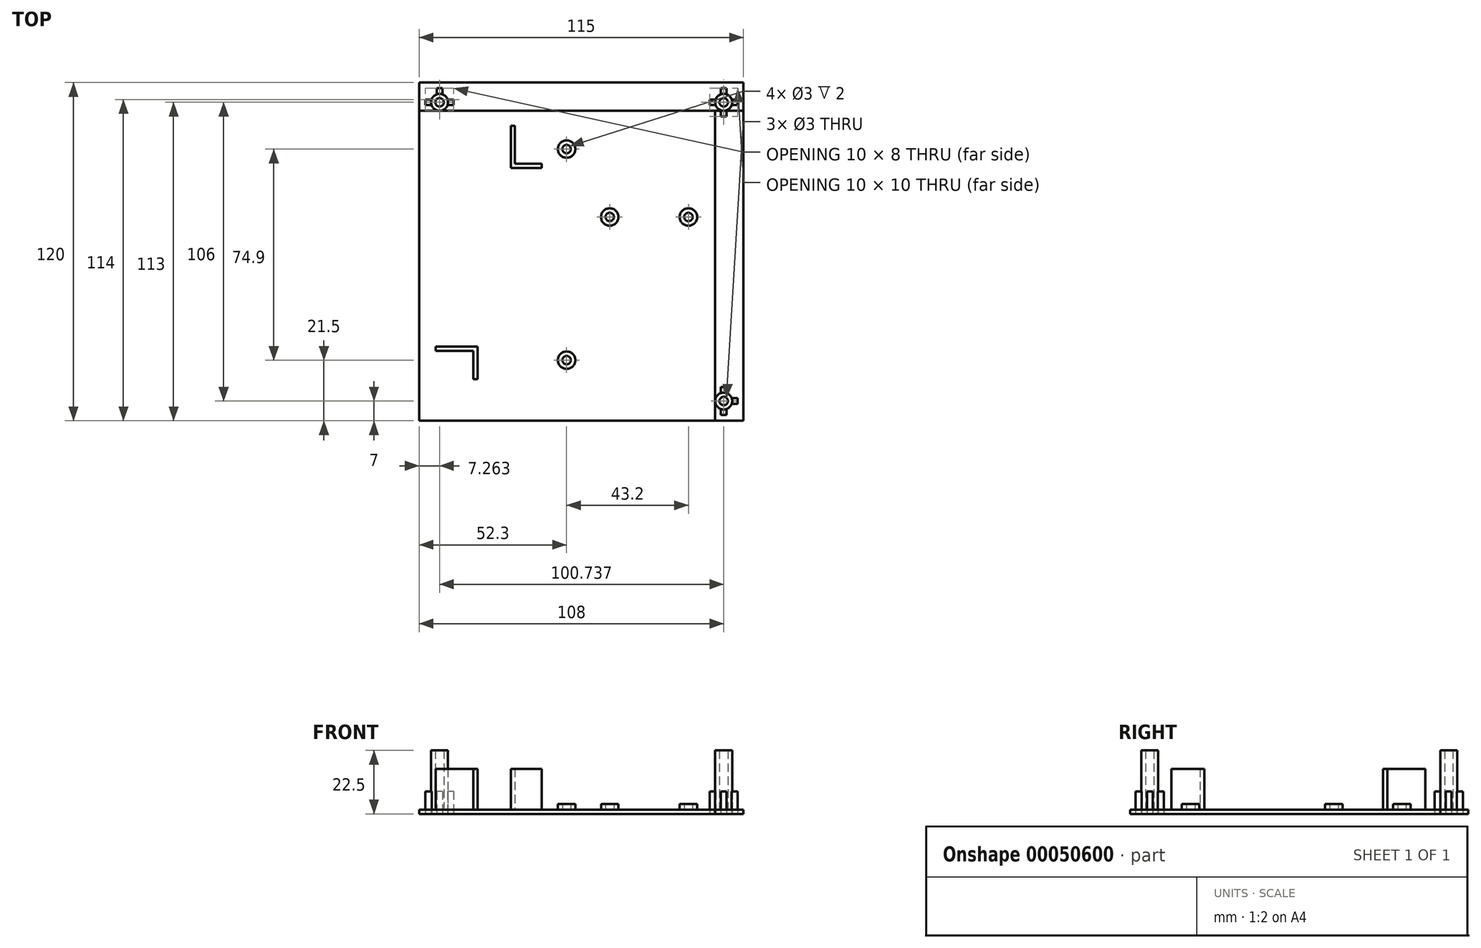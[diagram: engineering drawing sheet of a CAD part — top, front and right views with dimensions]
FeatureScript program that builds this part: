
annotation { "Feature Type Name" : "Feature", "Feature Type Description" : "" }
export const myFeature = defineFeature(function(context is Context, id is Id, definition is map)
    precondition{}
    {
        {
            var Q0;
            Q0=qCreatedBy(makeId("Top.planeOp"),FACE);
            var sketch = newSketch(context, id + "F0", { "sketchPlane" : qUnion([Q0])});
            skLineSegment(sketch, "E0.rect.bottom", {"start": v(52.5, 55) * mm, "end": v(-52.5, 55) * mm});
            skLineSegment(sketch, "E0.rect.top", {"start": v(52.5, -55) * mm, "end": v(-52.5, -55) * mm});
            skLineSegment(sketch, "E0.rect.left", {"start": v(52.5, 55) * mm, "end": v(52.5, -55) * mm});
            skLineSegment(sketch, "E0.rect.right", {"start": v(-52.5, 55) * mm, "end": v(-52.5, -55) * mm});
            skPoint(sketch, "E0.rect.middle", {"position": v(0, 0) * mm});
            skSolve(sketch);
        }
        {
            var Q0;
            Q0=makeQuery(id+"F0.imprint","IMPRINT",FACE,{"disambiguationData":[TD([[makeQuery(id+"F0.imprint","IMPRINT",EDGE,{"derivedFrom":sQuery(id+"F0.wireOp",EDGE,"E0.rect.bottom")}),1.0]])]});
            extrude(context, id + "F1", {"entities" : qUnion([Q0]), "depth" : 1.5 * mm});
        }
        {
            var Q0;
            Q0=makeQuery(id+"F1.opExtrude","CAP_FACE",FACE,{"disambiguationData":[OSD([sQuery(id+"F0.wireOp",EDGE,"E0.rect.bottom"),sQuery(id+"F0.wireOp",EDGE,"E0.rect.top"),sQuery(id+"F0.wireOp",EDGE,"E0.rect.left"),sQuery(id+"F0.wireOp",EDGE,"E0.rect.right")])],"isStart":false});
            var sketch = newSketch(context, id + "F2", { "sketchPlane" : qUnion([Q0])});
            skCircle(sketch, "E1", {"center": v(-0.2, 41.4) * mm, "radius": 3.1 * mm});
            skCircle(sketch, "E2", {"center": v(-0.2, 41.4) * mm, "radius": 1.5 * mm});
            skCircle(sketch, "E3", {"center": v(-0.2, -33.5) * mm, "radius": 3.1 * mm});
            skCircle(sketch, "E4", {"center": v(-0.2, -33.5) * mm, "radius": 1.5 * mm});
            skCircle(sketch, "E5", {"center": v(43, 17.3) * mm, "radius": 3.1 * mm});
            skCircle(sketch, "E6", {"center": v(43, 17.3) * mm, "radius": 1.5 * mm});
            skCircle(sketch, "E7", {"center": v(15.1, 17.3) * mm, "radius": 3.1 * mm});
            skCircle(sketch, "E8", {"center": v(15.1, 17.3) * mm, "radius": 1.5 * mm});
            skLineSegment(sketch, "E9", {"start": v(-20, 49.73) * mm, "end": v(-20, 34.73) * mm});
            skLineSegment(sketch, "E10", {"start": v(-20, 34.73) * mm, "end": v(-9, 34.73) * mm});
            skLineSegment(sketch, "E11", {"start": v(-9, 34.73) * mm, "end": v(-9, 36.23) * mm});
            skLineSegment(sketch, "E12", {"start": v(-9, 36.23) * mm, "end": v(-18.5, 36.23) * mm});
            skLineSegment(sketch, "E13", {"start": v(-18.5, 36.23) * mm, "end": v(-18.5, 49.73) * mm});
            skLineSegment(sketch, "E14", {"start": v(-18.5, 49.73) * mm, "end": v(-20, 49.73) * mm});
            skLineSegment(sketch, "E15", {"start": v(-46.6, -28.7) * mm, "end": v(-31.8, -28.7) * mm});
            skLineSegment(sketch, "E16", {"start": v(-31.8, -28.7) * mm, "end": v(-31.8, -40.3) * mm});
            skLineSegment(sketch, "E17", {"start": v(-31.8, -40.3) * mm, "end": v(-33.3, -40.3) * mm});
            skLineSegment(sketch, "E18", {"start": v(-33.3, -40.3) * mm, "end": v(-33.3, -30.2) * mm});
            skLineSegment(sketch, "E19", {"start": v(-33.3, -30.2) * mm, "end": v(-46.6, -30.2) * mm});
            skLineSegment(sketch, "E20", {"start": v(-46.6, -30.2) * mm, "end": v(-46.6, -28.7) * mm});
            skSolve(sketch);
        }
        {
            var Q0;
            Q0=makeQuery(id+"F2.imprint","IMPRINT",FACE,{"disambiguationData":[TD([[makeQuery(id+"F2.imprint","IMPRINT",EDGE,{"derivedFrom":sQuery(id+"F2.wireOp",EDGE,"E1")}),1.0]])]});
            var Q1;
            Q1=makeQuery(id+"F2.imprint","IMPRINT",FACE,{"disambiguationData":[TD([[makeQuery(id+"F2.imprint","IMPRINT",EDGE,{"derivedFrom":sQuery(id+"F2.wireOp",EDGE,"E7")}),1.0]])]});
            var Q2;
            Q2=makeQuery(id+"F2.imprint","IMPRINT",FACE,{"disambiguationData":[TD([[makeQuery(id+"F2.imprint","IMPRINT",EDGE,{"derivedFrom":sQuery(id+"F2.wireOp",EDGE,"E5")}),1.0]])]});
            var Q3;
            Q3=makeQuery(id+"F2.imprint","IMPRINT",FACE,{"disambiguationData":[TD([[makeQuery(id+"F2.imprint","IMPRINT",EDGE,{"derivedFrom":sQuery(id+"F2.wireOp",EDGE,"E3")}),1.0]])]});
            extrude(context, id + "F3", {"entities" : qUnion([Q0, Q1, Q2, Q3]), "operationType" : NewBodyOperationType.ADD, "depth" : 2 * mm});
        }
        {
            var Q0;
            Q0=makeQuery(id+"F2.imprint","IMPRINT",FACE,{"disambiguationData":[TD([[makeQuery(id+"F2.imprint","IMPRINT",EDGE,{"derivedFrom":sQuery(id+"F2.wireOp",EDGE,"E9")}),1.0]])]});
            extrude(context, id + "F4", {"entities" : qUnion([Q0]), "operationType" : NewBodyOperationType.ADD, "depth" : 14.5 * mm});
        }
        {
            var Q0;
            Q0=makeQuery(id+"F2.imprint","IMPRINT",FACE,{"disambiguationData":[TD([[makeQuery(id+"F2.imprint","IMPRINT",EDGE,{"derivedFrom":sQuery(id+"F2.wireOp",EDGE,"E15")}),-1.0]])]});
            extrude(context, id + "F5", {"entities" : qUnion([Q0]), "operationType" : NewBodyOperationType.ADD, "depth" : 14.5 * mm});
        }
        {
            var Q0;
            Q0=qCreatedBy(makeId("Top.planeOp"),FACE);
            var sketch = newSketch(context, id + "F6", { "sketchPlane" : qUnion([Q0])});
            skLineSegment(sketch, "E21.bottom", {"start": v(-52.5, 55) * mm, "end": v(62.5, 55) * mm});
            skLineSegment(sketch, "E21.top", {"start": v(-52.5, 65) * mm, "end": v(62.5, 65) * mm});
            skLineSegment(sketch, "E21.left", {"start": v(-52.5, 55) * mm, "end": v(-52.5, 65) * mm});
            skLineSegment(sketch, "E21.right", {"start": v(62.5, 55) * mm, "end": v(62.5, 65) * mm});
            skLineSegment(sketch, "E22.bottom", {"start": v(62.5, 55) * mm, "end": v(52.5, 55) * mm});
            skLineSegment(sketch, "E22.top", {"start": v(62.5, -55) * mm, "end": v(52.5, -55) * mm});
            skLineSegment(sketch, "E22.left", {"start": v(62.5, 55) * mm, "end": v(62.5, -55) * mm});
            skLineSegment(sketch, "E22.right", {"start": v(52.5, 55) * mm, "end": v(52.5, -55) * mm});
            skCircle(sketch, "E23", {"center": v(-45.24, 58) * mm, "radius": 3 * mm});
            skCircle(sketch, "E24", {"center": v(-45.24, 58) * mm, "radius": 1.5 * mm});
            skLineSegment(sketch, "E25.rect.bottom", {"start": v(-44.24, 63) * mm, "end": v(-46.24, 63) * mm});
            skLineSegment(sketch, "E25.rect.left", {"start": v(-44.24, 63) * mm, "end": v(-44.24, 60.83) * mm});
            skLineSegment(sketch, "E25.rect.right", {"start": v(-46.24, 63) * mm, "end": v(-46.24, 60.83) * mm});
            skPoint(sketch, "E25.rect.middle", {"position": v(-45.24, 61) * mm});
            skLineSegment(sketch, "E26.rect.right", {"start": v(-50.24, 59) * mm, "end": v(-50.24, 57) * mm});
            skPoint(sketch, "E26.rect.middle", {"position": v(-48.24, 58) * mm});
            skLineSegment(sketch, "E27.rect.bottom", {"start": v(-44.24, 53) * mm, "end": v(-46.24, 53) * mm});
            skLineSegment(sketch, "E27.rect.left", {"start": v(-44.24, 53) * mm, "end": v(-44.24, 55.17) * mm});
            skLineSegment(sketch, "E27.rect.right", {"start": v(-46.24, 53) * mm, "end": v(-46.24, 55.17) * mm});
            skPoint(sketch, "E27.rect.middle", {"position": v(-45.24, 55) * mm});
            skLineSegment(sketch, "E28.rect.bottom", {"start": v(-40.24, 59) * mm, "end": v(-42.4, 59) * mm});
            skLineSegment(sketch, "E28.rect.top", {"start": v(-40.24, 57) * mm, "end": v(-42.4, 57) * mm});
            skLineSegment(sketch, "E28.rect.left", {"start": v(-40.24, 59) * mm, "end": v(-40.24, 57) * mm});
            skPoint(sketch, "E28.rect.middle", {"position": v(-42.24, 58) * mm});
            skPoint(sketch, "E29.trimOffspring.end.orphan", {"position": v(-44.24, 57) * mm});
            skLineSegment(sketch, "E30.trimOffspring", {"start": v(-48.06, 57) * mm, "end": v(-50.24, 57) * mm});
            skPoint(sketch, "E26.rect.top.start.orphan", {"position": v(-46.24, 57) * mm});
            skLineSegment(sketch, "E31.trimOffspring", {"start": v(-48.06, 59) * mm, "end": v(-50.24, 59) * mm});
            skPoint(sketch, "E26.rect.bottom.start.orphan", {"position": v(-46.24, 59) * mm});
            skPoint(sketch, "E32.orphan", {"position": v(-44.24, 59) * mm});
            skCircle(sketch, "E33", {"center": v(55.5, 58) * mm, "radius": 3 * mm});
            skCircle(sketch, "E34", {"center": v(55.5, 58) * mm, "radius": 1.5 * mm});
            skLineSegment(sketch, "E35.rect.bottom", {"start": v(56.5, 63) * mm, "end": v(54.5, 63) * mm});
            skLineSegment(sketch, "E35.rect.left", {"start": v(56.5, 63) * mm, "end": v(56.5, 60.83) * mm});
            skLineSegment(sketch, "E35.rect.right", {"start": v(54.5, 63) * mm, "end": v(54.5, 60.83) * mm});
            skPoint(sketch, "E35.rect.middle", {"position": v(55.5, 61) * mm});
            skLineSegment(sketch, "E36.rect.bottom", {"start": v(60.5, 59) * mm, "end": v(58.33, 59) * mm});
            skLineSegment(sketch, "E36.rect.top", {"start": v(60.5, 57) * mm, "end": v(58.33, 57) * mm});
            skLineSegment(sketch, "E36.rect.left", {"start": v(60.5, 59) * mm, "end": v(60.5, 57) * mm});
            skPoint(sketch, "E36.rect.middle", {"position": v(58.5, 58) * mm});
            skLineSegment(sketch, "E37.rect.bottom", {"start": v(56.5, 53) * mm, "end": v(54.5, 53) * mm});
            skLineSegment(sketch, "E37.rect.left", {"start": v(56.5, 53) * mm, "end": v(56.5, 55.17) * mm});
            skLineSegment(sketch, "E37.rect.right", {"start": v(54.5, 53) * mm, "end": v(54.5, 55.17) * mm});
            skPoint(sketch, "E37.rect.middle", {"position": v(55.5, 55) * mm});
            skLineSegment(sketch, "E38.rect.right", {"start": v(50.5, 59) * mm, "end": v(50.5, 57) * mm});
            skPoint(sketch, "E38.rect.middle", {"position": v(52.5, 58) * mm});
            skLineSegment(sketch, "E39.trimOffspring", {"start": v(52.67, 59) * mm, "end": v(50.5, 59) * mm});
            skLineSegment(sketch, "E40.trimOffspring", {"start": v(52.67, 57) * mm, "end": v(50.5, 57) * mm});
            skPoint(sketch, "E38.rect.bottom.start.orphan", {"position": v(54.5, 59) * mm});
            skPoint(sketch, "E38.rect.top.start.orphan", {"position": v(54.5, 57) * mm});
            skPoint(sketch, "E41.trimOffspring.end.orphan", {"position": v(56.5, 57) * mm});
            skPoint(sketch, "E42.orphan", {"position": v(56.5, 59) * mm});
            skCircle(sketch, "E43", {"center": v(55.5, -48) * mm, "radius": 3 * mm});
            skCircle(sketch, "E44", {"center": v(55.5, -48) * mm, "radius": 1.5 * mm});
            skLineSegment(sketch, "E45.rect.bottom", {"start": v(56.5, -53) * mm, "end": v(54.5, -53) * mm});
            skLineSegment(sketch, "E45.rect.left", {"start": v(56.5, -53) * mm, "end": v(56.5, -50.83) * mm});
            skLineSegment(sketch, "E45.rect.right", {"start": v(54.5, -53) * mm, "end": v(54.5, -50.83) * mm});
            skPoint(sketch, "E45.rect.middle", {"position": v(55.5, -51) * mm});
            skLineSegment(sketch, "E46.rect.bottom", {"start": v(60.5, -47) * mm, "end": v(58.33, -47) * mm});
            skLineSegment(sketch, "E46.rect.top", {"start": v(60.5, -49) * mm, "end": v(58.33, -49) * mm});
            skLineSegment(sketch, "E46.rect.left", {"start": v(60.5, -47) * mm, "end": v(60.5, -49) * mm});
            skPoint(sketch, "E46.rect.middle", {"position": v(58.5, -48) * mm});
            skLineSegment(sketch, "E47.rect.bottom", {"start": v(56.5, -43) * mm, "end": v(54.5, -43) * mm});
            skLineSegment(sketch, "E47.rect.left", {"start": v(56.5, -43) * mm, "end": v(56.5, -45.17) * mm});
            skLineSegment(sketch, "E47.rect.right", {"start": v(54.5, -43) * mm, "end": v(54.5, -45.17) * mm});
            skPoint(sketch, "E47.rect.middle", {"position": v(55.5, -45) * mm});
            skLineSegment(sketch, "E48.rect.right", {"start": v(50.5, -47) * mm, "end": v(50.5, -49) * mm});
            skPoint(sketch, "E48.rect.middle", {"position": v(52.5, -48) * mm});
            skLineSegment(sketch, "E49.trimOffspring", {"start": v(52.67, -49) * mm, "end": v(50.5, -49) * mm});
            skPoint(sketch, "E48.rect.top.start.orphan", {"position": v(54.5, -49) * mm});
            skPoint(sketch, "E50.trimOffspring.end.orphan", {"position": v(56.5, -49) * mm});
            skLineSegment(sketch, "E51.trimOffspring", {"start": v(52.67, -47) * mm, "end": v(50.5, -47) * mm});
            skPoint(sketch, "E48.rect.bottom.start.orphan", {"position": v(54.5, -47) * mm});
            skPoint(sketch, "E52.trimOffspring.end.orphan", {"position": v(56.5, -47) * mm});
            skSolve(sketch);
        }
        {
            var Q0;
            Q0=makeQuery(id+"F6.imprint","IMPRINT",FACE,{"disambiguationData":[TD([[makeQuery(id+"F6.imprint","IMPRINT",EDGE,{"derivedFrom":sQuery(id+"F6.wireOp",EDGE,"E21.bottom")}),1.0]])]});
            var Q1;
            Q1=makeQuery(id+"F6.imprint","IMPRINT",FACE,{"disambiguationData":[TD([[makeQuery(id+"F6.imprint","IMPRINT",EDGE,{"derivedFrom":sQuery(id+"F6.wireOp",EDGE,"E22.bottom")}),1.0]])]});
            extrude(context, id + "F7", {"entities" : qUnion([Q0, Q1]), "operationType" : NewBodyOperationType.ADD, "depth" : 1.5 * mm});
        }
        {
            var Q0;
            Q0=makeQuery(id+"F6.imprint","IMPRINT",FACE,{"disambiguationData":[TD([[makeQuery(id+"F6.imprint","IMPRINT",EDGE,{"derivedFrom":sQuery(id+"F6.wireOp",EDGE,"E24")}),-1.0]])]});
            extrude(context, id + "F8", {"entities" : qUnion([Q0]), "depth" : 22.5 * mm});
        }
        {
            var Q0;
            Q0=makeQuery(id+"F6.imprint","IMPRINT",FACE,{"disambiguationData":[TD([[makeQuery(id+"F6.imprint","IMPRINT",EDGE,{"derivedFrom":sQuery(id+"F6.wireOp",EDGE,"E25.rect.bottom")}),1.0]])]});
            var Q1;
            Q1=makeQuery(id+"F6.imprint","IMPRINT",FACE,{"disambiguationData":[TD([[makeQuery(id+"F6.imprint","IMPRINT",EDGE,{"derivedFrom":sQuery(id+"F6.wireOp",EDGE,"E26.rect.right")}),1.0]])]});
            var Q2;
            {var subQ0=sQuery(id+"F6.wireOp",EDGE,"E28.rect.bottom");Q2=makeQuery(id+"F6.imprint","IMPRINT",FACE,{"disambiguationData":[TD([[makeQuery(id+"F6.imprint","IMPRINT",EDGE,{"derivedFrom":subQ0}),1.0]])]});}
            extrude(context, id + "F9", {"entities" : qUnion([Q0, Q1, Q2]), "depth" : 8 * mm});
        }
        {
            var Q0;
            Q0=makeQuery(id+"F6.imprint","IMPRINT",FACE,{"disambiguationData":[TD([[makeQuery(id+"F6.imprint","IMPRINT",EDGE,{"derivedFrom":sQuery(id+"F6.wireOp",EDGE,"E34")}),-1.0]])]});
            extrude(context, id + "F10", {"entities" : qUnion([Q0]), "depth" : 22.5 * mm});
        }
        {
            var Q0;
            Q0=makeQuery(id+"F6.imprint","IMPRINT",FACE,{"disambiguationData":[TD([[makeQuery(id+"F6.imprint","IMPRINT",EDGE,{"derivedFrom":sQuery(id+"F6.wireOp",EDGE,"E38.rect.right")}),1.0]])]});
            var Q1;
            Q1=makeQuery(id+"F6.imprint","IMPRINT",FACE,{"disambiguationData":[TD([[makeQuery(id+"F6.imprint","IMPRINT",EDGE,{"derivedFrom":sQuery(id+"F6.wireOp",EDGE,"E35.rect.bottom")}),1.0]])]});
            var Q2;
            {var subQ0=sQuery(id+"F6.wireOp",EDGE,"E36.rect.bottom");Q2=makeQuery(id+"F6.imprint","IMPRINT",FACE,{"disambiguationData":[TD([[makeQuery(id+"F6.imprint","IMPRINT",EDGE,{"derivedFrom":subQ0}),1.0]])]});}
            var Q3;
            {var subQ0=sQuery(id+"F6.wireOp",EDGE,"E37.rect.bottom");Q3=makeQuery(id+"F6.imprint","IMPRINT",FACE,{"disambiguationData":[TD([[makeQuery(id+"F6.imprint","IMPRINT",EDGE,{"derivedFrom":subQ0}),-1.0]])]});}
            extrude(context, id + "F11", {"entities" : qUnion([Q0, Q1, Q2, Q3]), "depth" : 8 * mm});
        }
        {
            var Q0;
            Q0=makeQuery(id+"F6.imprint","IMPRINT",FACE,{"disambiguationData":[TD([[makeQuery(id+"F6.imprint","IMPRINT",EDGE,{"derivedFrom":sQuery(id+"F6.wireOp",EDGE,"E21.top")}),-1.0]])]});
            var Q1;
            Q1=makeQuery(id+"F6.imprint","IMPRINT",FACE,{"disambiguationData":[TD([[makeQuery(id+"F6.imprint","IMPRINT",EDGE,{"derivedFrom":sQuery(id+"F6.wireOp",EDGE,"E22.top")}),-1.0]])]});
            extrude(context, id + "F12", {"entities" : qUnion([Q0, Q1]), "depth" : 1.5 * mm});
        }
        {
            var Q0;
            Q0=makeQuery(id+"F6.imprint","IMPRINT",FACE,{"disambiguationData":[TD([[makeQuery(id+"F6.imprint","IMPRINT",EDGE,{"derivedFrom":sQuery(id+"F6.wireOp",EDGE,"E44")}),-1.0]])]});
            extrude(context, id + "F13", {"entities" : qUnion([Q0]), "depth" : 22.5 * mm});
        }
        {
            var Q0;
            Q0=makeQuery(id+"F6.imprint","IMPRINT",FACE,{"disambiguationData":[TD([[makeQuery(id+"F6.imprint","IMPRINT",EDGE,{"derivedFrom":sQuery(id+"F6.wireOp",EDGE,"E47.rect.bottom")}),1.0]])]});
            var Q1;
            {var subQ0=sQuery(id+"F6.wireOp",EDGE,"E46.rect.bottom");Q1=makeQuery(id+"F6.imprint","IMPRINT",FACE,{"disambiguationData":[TD([[makeQuery(id+"F6.imprint","IMPRINT",EDGE,{"derivedFrom":subQ0}),1.0]])]});}
            var Q2;
            Q2=makeQuery(id+"F6.imprint","IMPRINT",FACE,{"disambiguationData":[TD([[makeQuery(id+"F6.imprint","IMPRINT",EDGE,{"derivedFrom":sQuery(id+"F6.wireOp",EDGE,"E45.rect.bottom")}),-1.0]])]});
            extrude(context, id + "F14", {"entities" : qUnion([Q0, Q1, Q2]), "depth" : 8 * mm});
        }
    });
